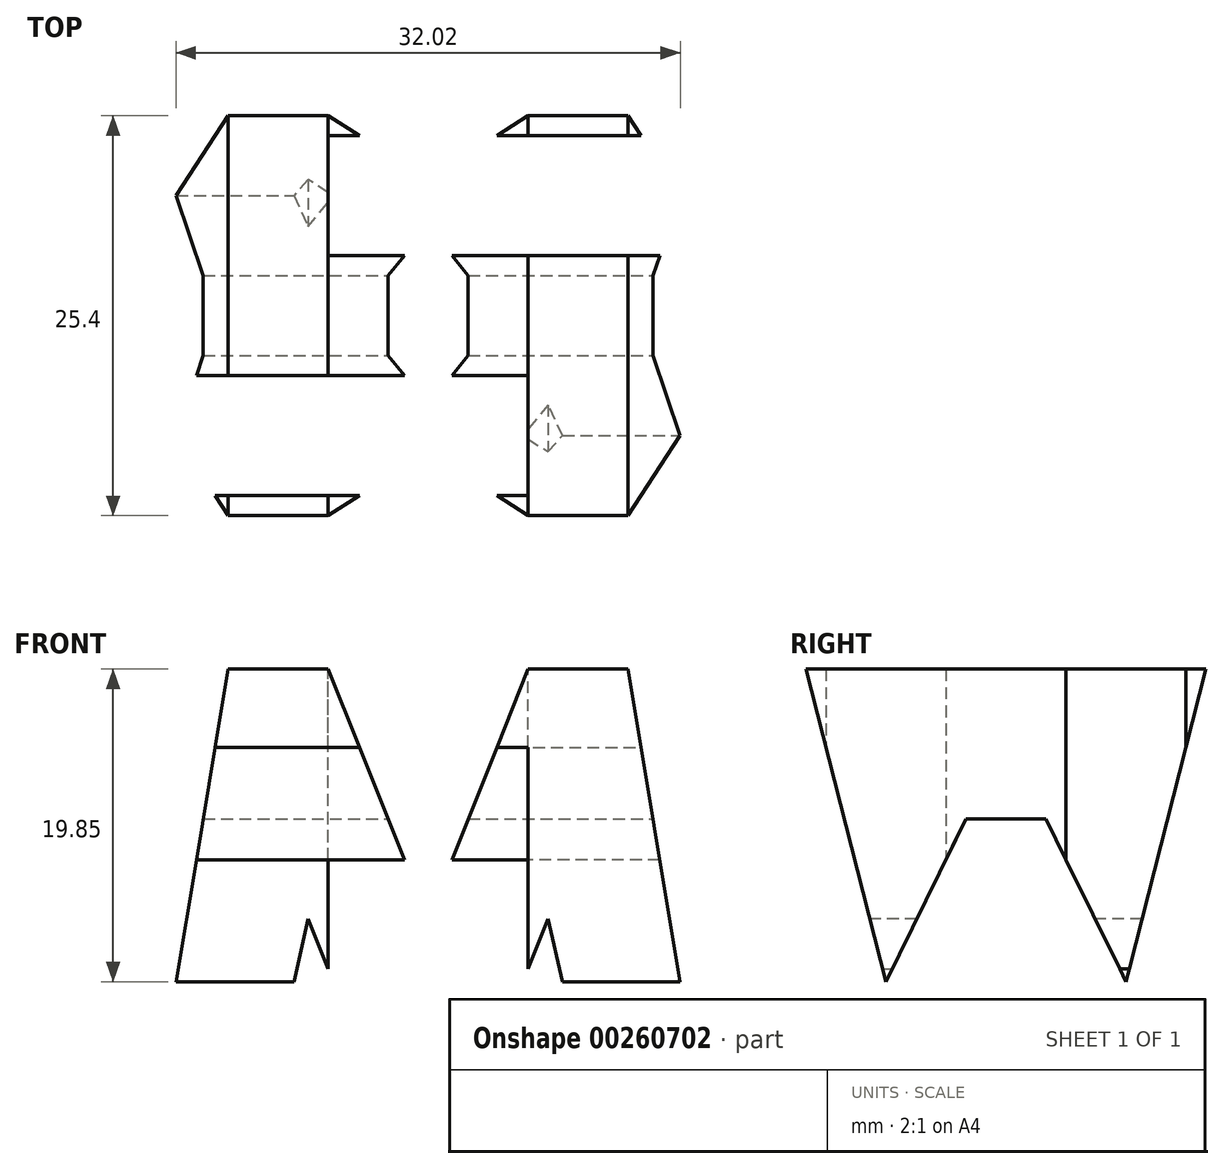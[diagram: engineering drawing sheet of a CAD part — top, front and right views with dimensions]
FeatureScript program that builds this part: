
annotation { "Feature Type Name" : "Feature", "Feature Type Description" : "" }
export const myFeature = defineFeature(function(context is Context, id is Id, definition is map)
    precondition{}
    {
        {
            var Q0;
            Q0=qCreatedBy(makeId("Front.planeOp"),FACE);
            var sketch = newSketch(context, id + "F0", { "sketchPlane" : qUnion([Q0])});
            skLineSegment(sketch, "E0", {"start": v(38.1, 0) * mm, "end": v(0, 0) * mm});
            skLineSegment(sketch, "E1", {"start": v(38.1, 0) * mm, "end": v(38.1, 38.1) * mm});
            skLineSegment(sketch, "E2", {"start": v(0, 38.1) * mm, "end": v(38.1, 38.1) * mm});
            skLineSegment(sketch, "E3", {"start": v(0, 38.1) * mm, "end": v(0, 0) * mm});
            skSolve(sketch);
        }
        {
            var Q0;
            Q0 = qSketchRegion(id + "F0", true);
            extrude(context, id + "F1", {"entities" : qUnion([Q0]), "depth" : 38.1 * mm});
        }
        {
            var Q0;
            Q0=qCreatedBy(makeId("Front.planeOp"),FACE);
            cPlane(context, id + "F2", {"entities" : qUnion([Q0]), "cplaneType" : CPlaneType.OFFSET, "offset" : 38.1 * mm, "width" : 152.4 * mm, "height" : 152.4 * mm});
        }
        {
            var Q0;
            Q0=qCreatedBy(makeId("Top.planeOp"),FACE);
            cPlane(context, id + "F3", {"entities" : qUnion([Q0]), "cplaneType" : CPlaneType.OFFSET, "offset" : 38.1 * mm, "width" : 152.4 * mm, "height" : 152.4 * mm});
        }
        {
            var Q0;
            Q0=makeQuery(id+"F1.opExtrude","SWEPT_FACE",FACE,{"disambiguationData":[OSD([sQuery(id+"F0.wireOp",EDGE,"E1")])]});
            var sketch = newSketch(context, id + "F4", { "sketchPlane" : qUnion([Q0])});
            skLineSegment(sketch, "E4", {"start": v(0, 0) * mm, "end": v(-38.1, 0) * mm});
            skLineSegment(sketch, "E5", {"start": v(-38.1, 0) * mm, "end": v(-38.1, 38.1) * mm});
            skLineSegment(sketch, "E6", {"start": v(-38.1, 38.1) * mm, "end": v(0, 38.1) * mm});
            skLineSegment(sketch, "E7", {"start": v(0, 38.1) * mm, "end": v(0, 0) * mm});
            skLineSegment(sketch, "E8", {"start": v(0, 38.1) * mm, "end": v(-6.35, 0) * mm});
            skLineSegment(sketch, "E9", {"start": v(-6.35, 0) * mm, "end": v(-12.7, 0) * mm});
            skLineSegment(sketch, "E10", {"start": v(-12.7, 0) * mm, "end": v(-19.05, 15.88) * mm});
            skLineSegment(sketch, "E11", {"start": v(-19.05, 15.88) * mm, "end": v(-25.4, 0) * mm});
            skLineSegment(sketch, "E12", {"start": v(-25.4, 0) * mm, "end": v(-31.75, 0) * mm});
            skLineSegment(sketch, "E13", {"start": v(-31.75, 0) * mm, "end": v(-38.1, 38.1) * mm});
            skLineSegment(sketch, "E14", {"start": v(-31.75, 38.1) * mm, "end": v(-26.67, 18.25) * mm});
            skLineSegment(sketch, "E15", {"start": v(-11.43, 18.25) * mm, "end": v(-6.35, 38.1) * mm});
            skLineSegment(sketch, "E16", {"start": v(-6.35, 38.1) * mm, "end": v(0, 38.1) * mm});
            skLineSegment(sketch, "E17", {"start": v(-31.75, 38.1) * mm, "end": v(-38.1, 38.1) * mm});
            skLineSegment(sketch, "E18", {"start": v(-26.67, 18.25) * mm, "end": v(-21.6, 28.58) * mm});
            skLineSegment(sketch, "E19", {"start": v(-21.6, 28.57) * mm, "end": v(-16.51, 28.57) * mm});
            skLineSegment(sketch, "E20", {"start": v(-16.51, 28.58) * mm, "end": v(-11.43, 18.25) * mm});
            skSolve(sketch);
        }
        {
            var Q0;
            Q0=makeQuery(id+"F4.imprint","IMPRINT",FACE,{"disambiguationData":[TD([[makeQuery(id+"F4.imprint","IMPRINT",EDGE,{"derivedFrom":sQuery(id+"F4.wireOp",EDGE,"E6")}),-1.0]])]});
            var Q1;
            {var subQ0=sQuery(id+"F4.wireOp",EDGE,"E7");Q1=makeQuery(id+"F4.imprint","IMPRINT",FACE,{"disambiguationData":[TD([[makeQuery(id+"F4.imprint","IMPRINT",EDGE,{"derivedFrom":subQ0}),1.0]])]});}
            var Q2;
            {var subQ0=sQuery(id+"F4.wireOp",EDGE,"E10");Q2=makeQuery(id+"F4.imprint","IMPRINT",FACE,{"disambiguationData":[TD([[makeQuery(id+"F4.imprint","IMPRINT",EDGE,{"derivedFrom":subQ0}),1.0]])]});}
            var Q3;
            {var subQ0=sQuery(id+"F4.wireOp",EDGE,"E5");Q3=makeQuery(id+"F4.imprint","IMPRINT",FACE,{"disambiguationData":[TD([[makeQuery(id+"F4.imprint","IMPRINT",EDGE,{"derivedFrom":subQ0}),-1.0]])]});}
            extrude(context, id + "F5", {"entities" : qUnion([Q0, Q1, Q2, Q3]), "operationType" : NewBodyOperationType.REMOVE, "oppositeDirection" : true, "depth" : 38.1 * mm});
        }
        {
            var Q0;
            Q0=qCreatedBy(id+"F2.planeOp",FACE);
            var sketch = newSketch(context, id + "F6", { "sketchPlane" : qUnion([Q0])});
            skLineSegment(sketch, "E21", {"start": v(0, 0) * mm, "end": v(0, 38.1) * mm});
            skLineSegment(sketch, "E22", {"start": v(0, 38.1) * mm, "end": v(38.1, 38.1) * mm});
            skLineSegment(sketch, "E23", {"start": v(0, 0) * mm, "end": v(38.1, 0) * mm});
            skLineSegment(sketch, "E24", {"start": v(38.1, 38.1) * mm, "end": v(38.1, 0) * mm});
            skLineSegment(sketch, "E25", {"start": v(0, 0) * mm, "end": v(6.35, 38.1) * mm});
            skLineSegment(sketch, "E26", {"start": v(12.7, 38.1) * mm, "end": v(19.05, 22.23) * mm});
            skLineSegment(sketch, "E27", {"start": v(19.05, 22.23) * mm, "end": v(25.4, 38.1) * mm});
            skLineSegment(sketch, "E28", {"start": v(31.75, 38.1) * mm, "end": v(38.1, 0) * mm});
            skLineSegment(sketch, "E29", {"start": v(6.35, 0) * mm, "end": v(11.43, 22.23) * mm});
            skLineSegment(sketch, "E30", {"start": v(11.43, 22.23) * mm, "end": v(16.51, 9.52) * mm});
            skLineSegment(sketch, "E31", {"start": v(16.51, 9.52) * mm, "end": v(21.59, 9.52) * mm});
            skLineSegment(sketch, "E32", {"start": v(21.59, 9.52) * mm, "end": v(26.67, 22.23) * mm});
            skLineSegment(sketch, "E33", {"start": v(26.67, 22.23) * mm, "end": v(31.75, 0) * mm});
            skSolve(sketch);
        }
        {
            var Q0;
            {var subQ0=sQuery(id+"F6.wireOp",EDGE,"E26");Q0=makeQuery(id+"F6.imprint","IMPRINT",FACE,{"disambiguationData":[TD([[makeQuery(id+"F6.imprint","IMPRINT",EDGE,{"derivedFrom":subQ0}),1.0]])]});}
            var Q1;
            {var subQ0=sQuery(id+"F6.wireOp",EDGE,"E29");Q1=makeQuery(id+"F6.imprint","IMPRINT",FACE,{"disambiguationData":[TD([[makeQuery(id+"F6.imprint","IMPRINT",EDGE,{"derivedFrom":subQ0}),-1.0]])]});}
            var Q2;
            {var subQ0=sQuery(id+"F6.wireOp",EDGE,"E21");Q2=makeQuery(id+"F6.imprint","IMPRINT",FACE,{"disambiguationData":[TD([[makeQuery(id+"F6.imprint","IMPRINT",EDGE,{"derivedFrom":subQ0}),-1.0]])]});}
            var Q3;
            {var subQ0=sQuery(id+"F6.wireOp",EDGE,"E24");Q3=makeQuery(id+"F6.imprint","IMPRINT",FACE,{"disambiguationData":[TD([[makeQuery(id+"F6.imprint","IMPRINT",EDGE,{"derivedFrom":subQ0}),-1.0]])]});}
            extrude(context, id + "F7", {"entities" : qUnion([Q0, Q1, Q2, Q3]), "operationType" : NewBodyOperationType.REMOVE, "oppositeDirection" : true, "depth" : 38.1 * mm});
        }
        {
            var Q0;
            Q0=qCreatedBy(id+"F3.planeOp",FACE);
            var sketch = newSketch(context, id + "F8", { "sketchPlane" : qUnion([Q0])});
            skLineSegment(sketch, "E34", {"start": v(0, 0) * mm, "end": v(0, -38.1) * mm});
            skLineSegment(sketch, "E35", {"start": v(0, -38.1) * mm, "end": v(38.1, -38.1) * mm});
            skLineSegment(sketch, "E36", {"start": v(38.1, -38.1) * mm, "end": v(38.1, 0) * mm});
            skLineSegment(sketch, "E37", {"start": v(38.1, 0) * mm, "end": v(0, 0) * mm});
            skLineSegment(sketch, "E38", {"start": v(38.1, -7.62) * mm, "end": v(12.7, -7.62) * mm});
            skLineSegment(sketch, "E39", {"start": v(12.7, -7.62) * mm, "end": v(12.7, -15.24) * mm});
            skLineSegment(sketch, "E40", {"start": v(12.7, -15.24) * mm, "end": v(38.1, -15.24) * mm});
            skLineSegment(sketch, "E41", {"start": v(0, -22.86) * mm, "end": v(25.4, -22.86) * mm});
            skLineSegment(sketch, "E42", {"start": v(25.4, -22.86) * mm, "end": v(25.4, -30.48) * mm});
            skLineSegment(sketch, "E43", {"start": v(25.4, -30.48) * mm, "end": v(0, -30.48) * mm});
            skSolve(sketch);
        }
        {
            var Q0;
            {var subQ0=sQuery(id+"F8.wireOp",EDGE,"E38");Q0=makeQuery(id+"F8.imprint","IMPRINT",FACE,{"disambiguationData":[TD([[makeQuery(id+"F8.imprint","IMPRINT",EDGE,{"derivedFrom":subQ0}),1.0]])]});}
            var Q1;
            {var subQ0=sQuery(id+"F8.wireOp",EDGE,"E41");Q1=makeQuery(id+"F8.imprint","IMPRINT",FACE,{"disambiguationData":[TD([[makeQuery(id+"F8.imprint","IMPRINT",EDGE,{"derivedFrom":subQ0}),-1.0]])]});}
            extrude(context, id + "F9", {"entities" : qUnion([Q0, Q1]), "operationType" : NewBodyOperationType.REMOVE, "oppositeDirection" : true, "depth" : 38.1 * mm});
        }
    });
